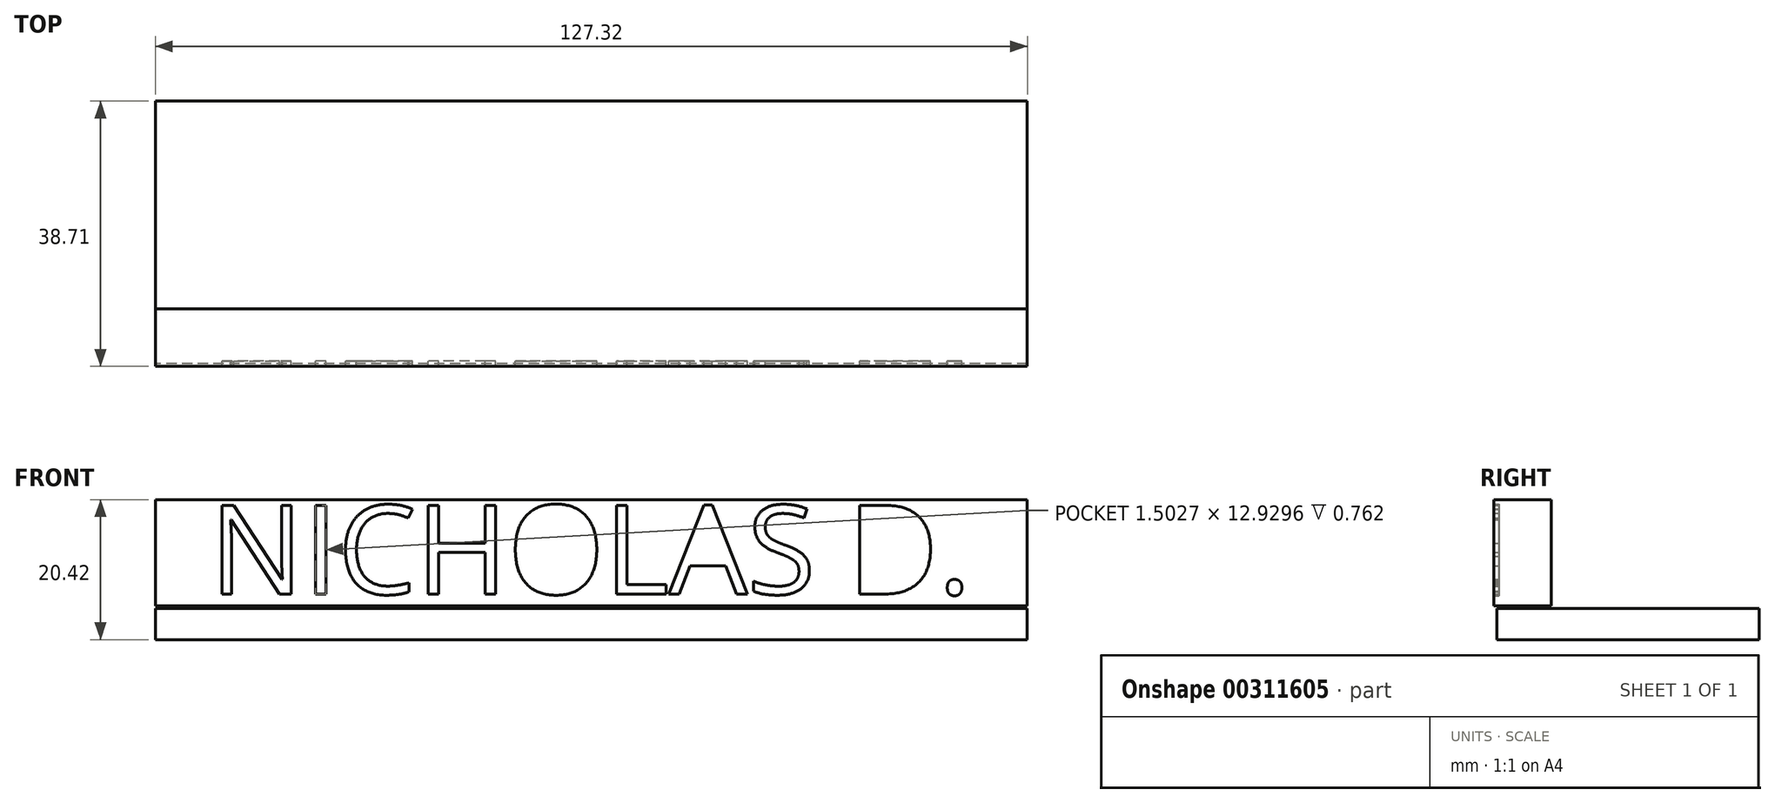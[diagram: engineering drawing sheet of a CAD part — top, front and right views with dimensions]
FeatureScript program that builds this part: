
annotation { "Feature Type Name" : "Feature", "Feature Type Description" : "" }
export const myFeature = defineFeature(function(context is Context, id is Id, definition is map)
    precondition{}
    {
        {
            var Q0;
            Q0=qCreatedBy(makeId("Top.planeOp"),FACE);
            var sketch = newSketch(context, id + "F0", { "sketchPlane" : qUnion([Q0])});
            skLineSegment(sketch, "E0.bottom", {"start": v(63.66, -19.15) * mm, "end": v(-63.66, -19.15) * mm});
            skLineSegment(sketch, "E0.top", {"start": v(63.66, 19.15) * mm, "end": v(-63.66, 19.15) * mm});
            skLineSegment(sketch, "E0.left", {"start": v(63.66, -19.15) * mm, "end": v(63.66, 19.15) * mm});
            skLineSegment(sketch, "E0.right", {"start": v(-63.66, -19.15) * mm, "end": v(-63.66, 19.15) * mm});
            skPoint(sketch, "E0.middle", {"position": v(0, 0) * mm});
            skSolve(sketch);
        }
        {
            var Q0;
            Q0=makeQuery(id+"F0.imprint","IMPRINT",FACE,{"disambiguationData":[TD([[makeQuery(id+"F0.imprint","IMPRINT",EDGE,{"derivedFrom":sQuery(id+"F0.wireOp",EDGE,"E0.bottom")}),-1.0]])]});
            extrude(context, id + "F1", {"entities" : qUnion([Q0]), "depth" : 3.56 * mm, "hasSecondDirection" : true, "secondDirectionOppositeDirection" : true, "secondDirectionDepth" : 1.02 * mm});
        }
        {
            var Q0;
            Q0=qCreatedBy(makeId("Front.planeOp"),FACE);
            var sketch = newSketch(context, id + "F2", { "sketchPlane" : qUnion([Q0])});
            skLineSegment(sketch, "E1.bottom", {"start": v(63.65, 3.88) * mm, "end": v(-63.65, 3.88) * mm});
            skLineSegment(sketch, "E1.top", {"start": v(63.65, 19.4) * mm, "end": v(-63.65, 19.4) * mm});
            skLineSegment(sketch, "E1.left", {"start": v(63.65, 3.88) * mm, "end": v(63.65, 19.4) * mm});
            skLineSegment(sketch, "E1.right", {"start": v(-63.65, 3.88) * mm, "end": v(-63.65, 19.4) * mm});
            skPoint(sketch, "E1.middle", {"position": v(0, 11.64) * mm});
            skSolve(sketch);
        }
        {
            var Q0;
            Q0=makeQuery(id+"F2.imprint","IMPRINT",FACE,{"disambiguationData":[TD([[makeQuery(id+"F2.imprint","IMPRINT",EDGE,{"derivedFrom":sQuery(id+"F2.wireOp",EDGE,"E1.bottom")}),-1.0]])]});
            extrude(context, id + "F3", {"entities" : qUnion([Q0]), "depth" : 18.8 * mm, "hasSecondDirection" : true, "secondDirectionOppositeDirection" : false, "secondDirectionDepth" : 11.18 * mm});
        }
        {
            var Q0;
            Q0=makeQuery(id+"F3.opExtrude","CAP_FACE",FACE,{"disambiguationData":[OSD([sQuery(id+"F2.wireOp",EDGE,"E1.bottom"),sQuery(id+"F2.wireOp",EDGE,"E1.top"),sQuery(id+"F2.wireOp",EDGE,"E1.left"),sQuery(id+"F2.wireOp",EDGE,"E1.right")])],"isStart":false});
            var sketch = newSketch(context, id + "F4", { "sketchPlane" : qUnion([Q0])});
            skText(sketch, "E2", { "text": "NICHOLAS D.", "fontName": "OpenSans-Regular.ttf"});
            const initialGuessF4  = {"E2": [-0.05569, 0.00564, 1, 0, 0.01304]};
            skSetInitialGuess(sketch, initialGuessF4);
            skSolve(sketch);
        }
        {
            var Q0;
            Q0=makeQuery(id+"F4.imprint","IMPRINT",FACE,{"disambiguationData":[TD([[makeQuery(id+"F4.imprint","IMPRINT",EDGE,{"derivedFrom":sQuery(id+"F4.wireOp",EDGE,"E2.sketch_text.stroke-0")}),1.0]])]});
            extrude(context, id + "F5", {"entities" : qUnion([Q0]), "operationType" : NewBodyOperationType.ADD, "depth" : 0.76 * mm});
        }
    });
